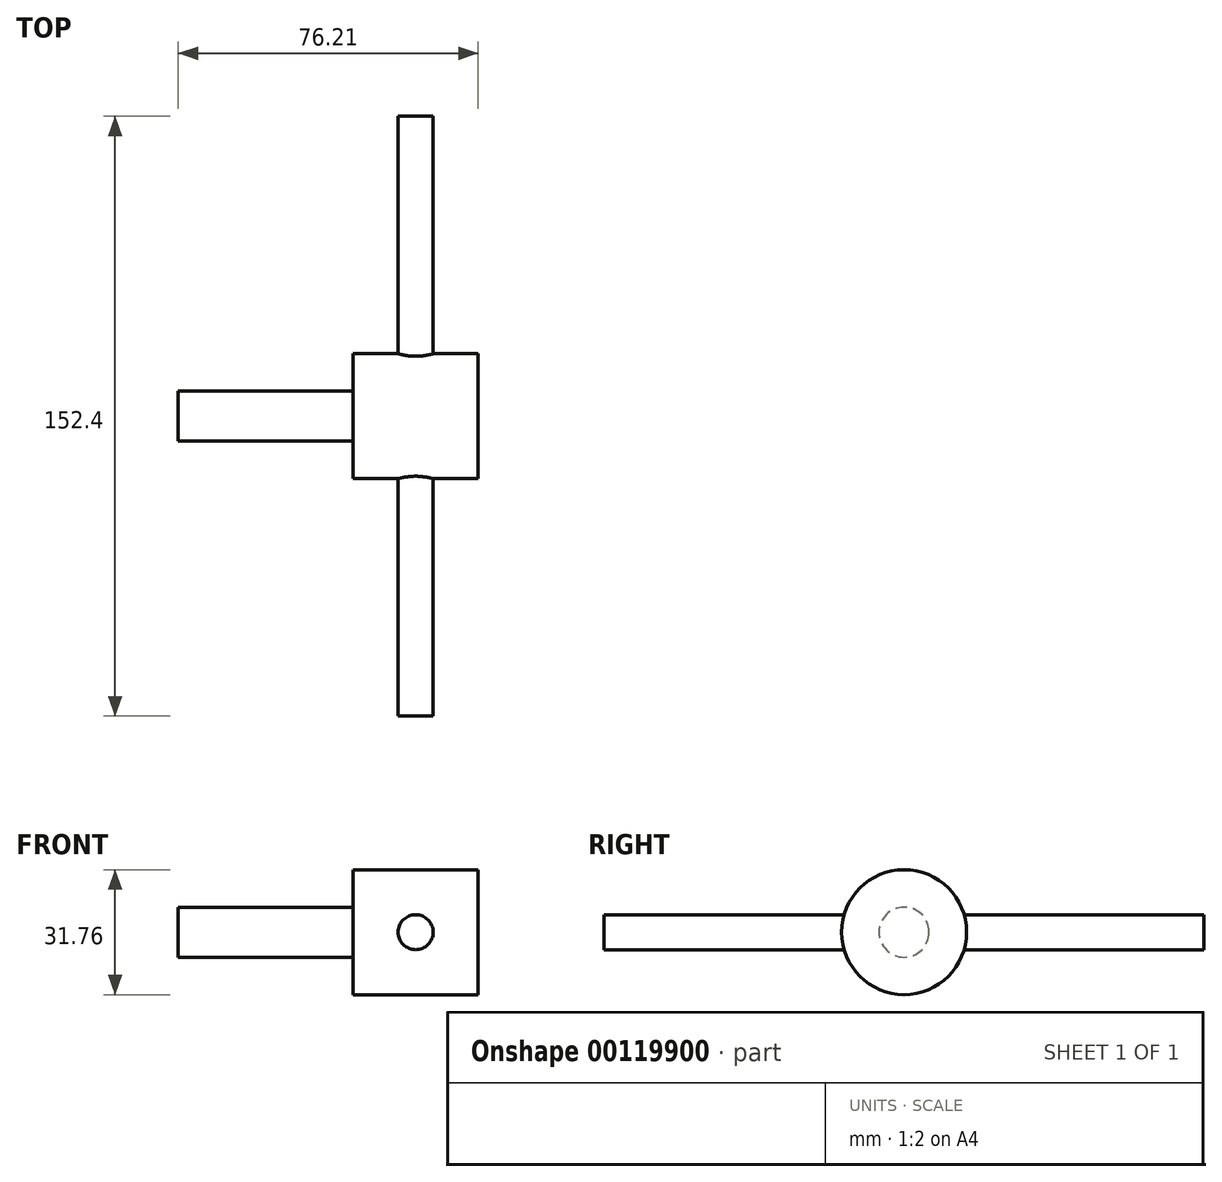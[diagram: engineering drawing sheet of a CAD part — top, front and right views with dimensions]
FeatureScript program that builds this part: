
annotation { "Feature Type Name" : "Feature", "Feature Type Description" : "" }
export const myFeature = defineFeature(function(context is Context, id is Id, definition is map)
    precondition{}
    {
        {
            var Q0;
            Q0=qCreatedBy(makeId("Right.planeOp"),FACE);
            var sketch = newSketch(context, id + "F0", { "sketchPlane" : qUnion([Q0])});
            skLineSegment(sketch, "E0", {"start": v(-93.66, 0) * mm, "end": v(100.73, 0) * mm, "construction": true});
            skCircle(sketch, "E1", {"center": v(0, 0) * mm, "radius": 15.88 * mm});
            skSolve(sketch);
        }
        {
            var Q0;
            Q0=makeQuery(id+"F0.imprint","IMPRINT",FACE,{"disambiguationData":[TD([[makeQuery(id+"F0.imprint","IMPRINT",EDGE,{"derivedFrom":sQuery(id+"F0.wireOp",EDGE,"E1")}),1.0]])]});
            extrude(context, id + "F1", {"entities" : qUnion([Q0]), "endBound" : BoundingType.SYMMETRIC, "depth" : 31.75 * mm});
        }
        {
            var Q0;
            Q0=makeQuery(id+"F1.opExtrude","CAP_FACE",FACE,{"disambiguationData":[OSD([sQuery(id+"F0.wireOp",EDGE,"E1")])],"isStart":true});
            var sketch = newSketch(context, id + "F2", { "sketchPlane" : qUnion([Q0])});
            skCircle(sketch, "E2", {"center": v(0, 0) * mm, "radius": 6.35 * mm});
            skSolve(sketch);
        }
        {
            var Q0;
            Q0=makeQuery(id+"F2.imprint","IMPRINT",FACE,{"disambiguationData":[TD([[makeQuery(id+"F2.imprint","IMPRINT",EDGE,{"derivedFrom":sQuery(id+"F2.wireOp",EDGE,"E2")}),1.0]])]});
            extrude(context, id + "F3", {"entities" : qUnion([Q0]), "operationType" : NewBodyOperationType.ADD, "depth" : 44.45 * mm});
        }
        {
            var Q0;
            Q0=qCreatedBy(makeId("Front.planeOp"),FACE);
            var sketch = newSketch(context, id + "F4", { "sketchPlane" : qUnion([Q0])});
            skCircle(sketch, "E3", {"center": v(0, 0) * mm, "radius": 4.45 * mm});
            skSolve(sketch);
        }
        {
            var Q0;
            Q0 = qSketchRegion(id + "F4", true);
            extrude(context, id + "F5", {"entities" : qUnion([Q0]), "operationType" : NewBodyOperationType.ADD, "endBound" : BoundingType.SYMMETRIC, "depth" : 152.4 * mm});
        }
        {
            var Q0;
            Q0=makeQuery(id+"F5.opExtrude","CAP_FACE",FACE,{"disambiguationData":[OSD([sQuery(id+"F4.wireOp",EDGE,"E3")])],"isStart":false});
            var sketch = newSketch(context, id + "F6", { "sketchPlane" : qUnion([Q0])});
            skSolve(sketch);
        }
        {
            var Q0;
            Q0=makeQuery(id+"F6.imprint","IMPRINT",FACE,{"disambiguationData":[TD([[makeQuery(id+"F6.imprint","IMPRINT",EDGE,{"derivedFrom":makeQuery(id+"F5.opExtrude","CAP_EDGE",EDGE,{"disambiguationData":[OSD([sQuery(id+"F4.wireOp",EDGE,"E3")])],"isStart":false})}),1.0]])]});
            var sketch = newSketch(context, id + "F7", { "sketchPlane" : qUnion([Q0])});
            skLineSegment(sketch, "E4", {"start": v(33.41, 0) * mm, "end": v(-26.03, 0) * mm, "construction": true});
            skArc(sketch, "E5", {"start": v(-10.3, 0) * mm, "mid": v(-0.14, -10.16) * mm, "end": v(10.02, 0) * mm});
            skSolve(sketch);
        }
        {
            var Q0;
            Q0=makeQuery(id+"F5.opExtrude","CAP_FACE",FACE,{"disambiguationData":[OSD([sQuery(id+"F4.wireOp",EDGE,"E3")])],"isStart":true});
            var sketch = newSketch(context, id + "F8", { "sketchPlane" : qUnion([Q0])});
            skLineSegment(sketch, "E6", {"start": v(43.97, 0) * mm, "end": v(-34.04, 0) * mm, "construction": true});
            skArc(sketch, "E7", {"start": v(-10.16, 0) * mm, "mid": v(0, -10.16) * mm, "end": v(10.16, 0) * mm});
            skSolve(sketch);
        }
        {
            var Q0;
            Q0=sQuery(id+"F7.wireOp",EDGE,"E5");
            var Q1;
            Q1=sQuery(id+"F7.wireOp",EDGE,"E4");
            revolve(context, id + "F9", {"bodyType" : ToolBodyType.SURFACE, "surfaceEntities" : qUnion([Q0]), "axis" : qUnion([Q1]), "revolveType" : RevolveType.FULL});
        }
        {
            var Q0;
            Q0=sQuery(id+"F8.wireOp",EDGE,"E7");
            var Q1;
            Q1=sQuery(id+"F8.wireOp",EDGE,"E6");
            revolve(context, id + "F10", {"bodyType" : ToolBodyType.SURFACE, "surfaceEntities" : qUnion([Q0]), "axis" : qUnion([Q1]), "revolveType" : RevolveType.FULL});
        }
    });
